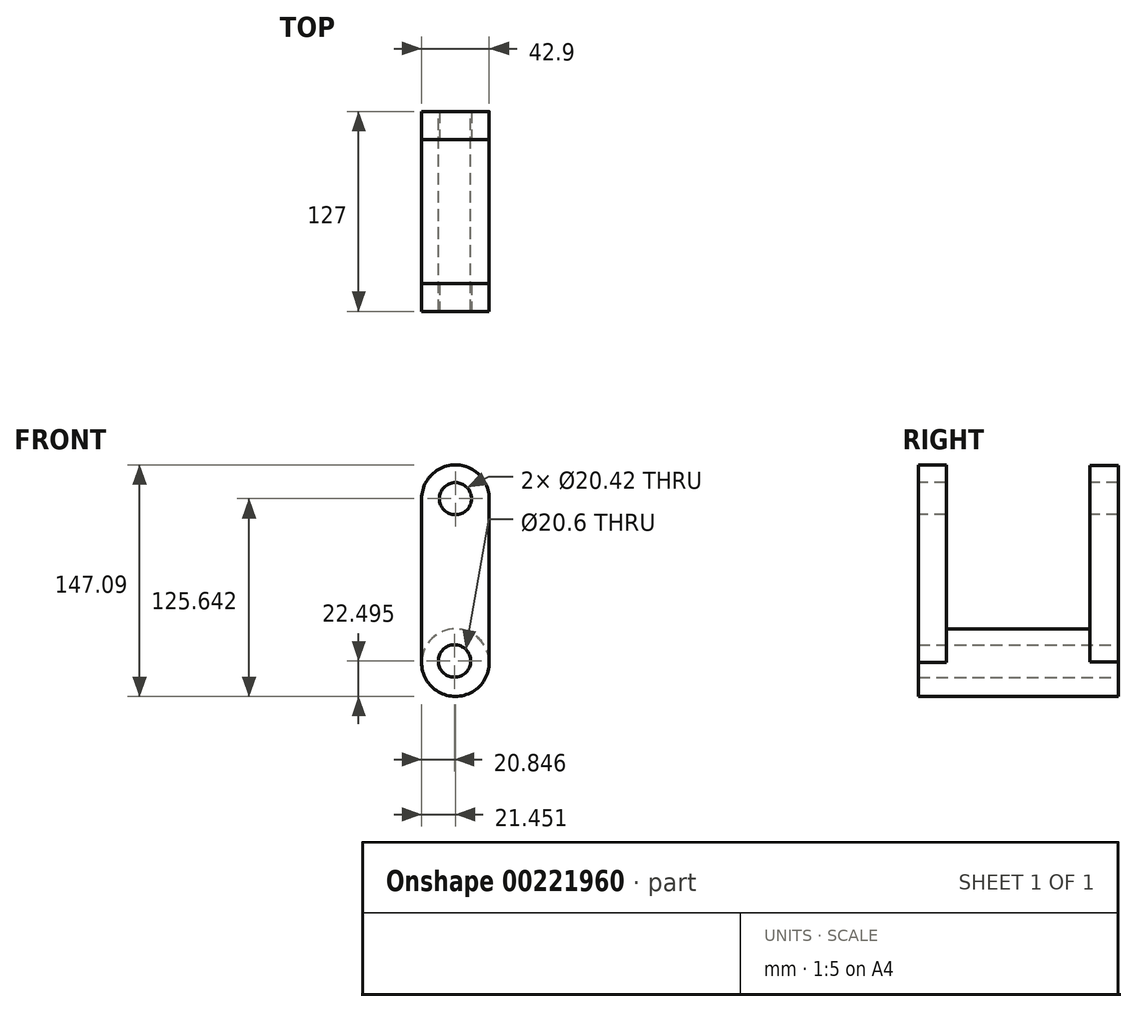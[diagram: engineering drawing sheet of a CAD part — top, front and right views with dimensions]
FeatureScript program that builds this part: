
annotation { "Feature Type Name" : "Feature", "Feature Type Description" : "" }
export const myFeature = defineFeature(function(context is Context, id is Id, definition is map)
    precondition{}
    {
        {
            var Q0;
            Q0=qCreatedBy(makeId("Front.planeOp"),FACE);
            var sketch = newSketch(context, id + "F0", { "sketchPlane" : qUnion([Q0])});
            skCircle(sketch, "E0", {"center": v(25.16, 31.72) * mm, "radius": 21.42 * mm});
            skSolve(sketch);
        }
        {
            var Q0;
            Q0 = qSketchRegion(id + "F0", true);
            extrude(context, id + "F1", {"entities" : qUnion([Q0]), "depth" : 127 * mm});
        }
        {
            var Q0;
            Q0=makeQuery(id+"F1.opExtrude","CAP_FACE",FACE,{"disambiguationData":[OSD([sQuery(id+"F0.wireOp",EDGE,"E0")])],"isStart":true});
            var sketch = newSketch(context, id + "F2", { "sketchPlane" : qUnion([Q0])});
            skLineSegment(sketch, "E1", {"start": v(-3.75, 32.24) * mm, "end": v(-46.57, 32.24) * mm});
            skLineSegment(sketch, "E2", {"start": v(-46.57, 32.24) * mm, "end": v(-46.57, 135.51) * mm});
            skLineSegment(sketch, "E3", {"start": v(-46.57, 135.51) * mm, "end": v(-3.75, 135.51) * mm});
            skLineSegment(sketch, "E4", {"start": v(-3.75, 135.51) * mm, "end": v(-3.75, 32.24) * mm});
            skSolve(sketch);
        }
        {
            var Q0;
            Q0 = qSketchRegion(id + "F2", true);
            extrude(context, id + "F3", {"entities" : qUnion([Q0]), "operationType" : NewBodyOperationType.ADD, "oppositeDirection" : true, "depth" : 17.78 * mm});
        }
        {
            var Q0;
            Q0=makeQuery(id+"F1.opExtrude","CAP_FACE",FACE,{"disambiguationData":[OSD([sQuery(id+"F0.wireOp",EDGE,"E0")])],"isStart":false});
            var sketch = newSketch(context, id + "F4", { "sketchPlane" : qUnion([Q0])});
            skLineSegment(sketch, "E5", {"start": v(46.58, 31.96) * mm, "end": v(3.75, 31.96) * mm});
            skLineSegment(sketch, "E6", {"start": v(3.75, 31.96) * mm, "end": v(3.75, 135.93) * mm});
            skLineSegment(sketch, "E7", {"start": v(3.75, 135.93) * mm, "end": v(46.64, 135.93) * mm});
            skLineSegment(sketch, "E8", {"start": v(46.64, 135.93) * mm, "end": v(46.58, 31.96) * mm});
            skSolve(sketch);
        }
        {
            var Q0;
            Q0 = qSketchRegion(id + "F4", true);
            extrude(context, id + "F5", {"entities" : qUnion([Q0]), "operationType" : NewBodyOperationType.ADD, "oppositeDirection" : true, "depth" : 17.78 * mm});
        }
        {
            var Q0;
            Q0=qCreatedBy(makeId("Front.planeOp"),FACE);
            var sketch = newSketch(context, id + "F6", { "sketchPlane" : qUnion([Q0])});
            skCircle(sketch, "E9", {"center": v(25.24, 31.5) * mm, "radius": 7.37 * mm});
            skSolve(sketch);
        }
        {
            var Q0;
            Q0 = qSketchRegion(id + "F6", true);
            extrude(context, id + "F7", {"entities" : qUnion([Q0]), "operationType" : NewBodyOperationType.REMOVE, "endBound" : BoundingType.THROUGH_ALL, "oppositeDirection" : true, "depth" : 25.4 * mm});
        }
        {
            var Q0;
            Q0=qCreatedBy(makeId("Front.planeOp"),FACE);
            var sketch = newSketch(context, id + "F8", { "sketchPlane" : qUnion([Q0])});
            skCircle(sketch, "E10", {"center": v(24.59, 32.8) * mm, "radius": 10.3 * mm});
            skSolve(sketch);
        }
        {
            var Q0;
            Q0 = qSketchRegion(id + "F8", true);
            extrude(context, id + "F9", {"entities" : qUnion([Q0]), "operationType" : NewBodyOperationType.REMOVE, "endBound" : BoundingType.THROUGH_ALL, "depth" : 25.4 * mm});
        }
        {
            var Q0;
            Q0=makeQuery(id+"F5.boolean.opBoolean","MERGE",FACE,{"derivedFrom":[makeQuery(id+"F1.opExtrude","CAP_FACE",FACE,{"disambiguationData":[OSD([sQuery(id+"F0.wireOp",EDGE,"E0")])],"isStart":false}),makeQuery(id+"F5.opExtrude","CAP_FACE",FACE,{"disambiguationData":[OSD([sQuery(id+"F4.wireOp",EDGE,"E5"),sQuery(id+"F4.wireOp",EDGE,"E6"),sQuery(id+"F4.wireOp",EDGE,"E7"),sQuery(id+"F4.wireOp",EDGE,"E8")])],"isStart":true})]});
            var sketch = newSketch(context, id + "F10", { "sketchPlane" : qUnion([Q0])});
            skArc(sketch, "E11", {"start": v(46.64, 135.93) * mm, "mid": v(25.2, 157.39) * mm, "end": v(3.75, 135.93) * mm});
            skLineSegment(sketch, "E12", {"start": v(3.75, 135.93) * mm, "end": v(46.64, 135.93) * mm});
            skSolve(sketch);
        }
        {
            var Q0;
            Q0 = qSketchRegion(id + "F10", true);
            extrude(context, id + "F11", {"entities" : qUnion([Q0]), "operationType" : NewBodyOperationType.ADD, "oppositeDirection" : true, "depth" : 17.78 * mm});
        }
        {
            var Q0;
            Q0=makeQuery(id+"F3.boolean.opBoolean","MERGE",FACE,{"derivedFrom":[makeQuery(id+"F1.opExtrude","CAP_FACE",FACE,{"disambiguationData":[OSD([sQuery(id+"F0.wireOp",EDGE,"E0")])],"isStart":true}),makeQuery(id+"F3.opExtrude","CAP_FACE",FACE,{"disambiguationData":[OSD([sQuery(id+"F2.wireOp",EDGE,"E1"),sQuery(id+"F2.wireOp",EDGE,"E2"),sQuery(id+"F2.wireOp",EDGE,"E3"),sQuery(id+"F2.wireOp",EDGE,"E4")])],"isStart":true})]});
            var sketch = newSketch(context, id + "F12", { "sketchPlane" : qUnion([Q0])});
            skArc(sketch, "E13", {"start": v(-3.75, 135.51) * mm, "mid": v(-25.16, 156.92) * mm, "end": v(-46.57, 135.51) * mm});
            skLineSegment(sketch, "E14", {"start": v(-46.57, 135.51) * mm, "end": v(-3.75, 135.51) * mm});
            skSolve(sketch);
        }
        {
            var Q0;
            Q0 = qSketchRegion(id + "F12", true);
            extrude(context, id + "F13", {"entities" : qUnion([Q0]), "operationType" : NewBodyOperationType.ADD, "oppositeDirection" : true, "depth" : 17.78 * mm});
        }
        {
            var Q0;
            Q0=makeQuery(id+"F11.boolean.opBoolean","MERGE",FACE,{"derivedFrom":[makeQuery(id+"F5.boolean.opBoolean","MERGE",FACE,{"derivedFrom":[makeQuery(id+"F1.opExtrude","CAP_FACE",FACE,{"disambiguationData":[OSD([sQuery(id+"F0.wireOp",EDGE,"E0")])],"isStart":false}),makeQuery(id+"F5.opExtrude","CAP_FACE",FACE,{"disambiguationData":[OSD([sQuery(id+"F4.wireOp",EDGE,"E5"),sQuery(id+"F4.wireOp",EDGE,"E6"),sQuery(id+"F4.wireOp",EDGE,"E7"),sQuery(id+"F4.wireOp",EDGE,"E8")])],"isStart":true})]}),makeQuery(id+"F11.opExtrude","CAP_FACE",FACE,{"disambiguationData":[OSD([sQuery(id+"F10.wireOp",EDGE,"E11"),sQuery(id+"F10.wireOp",EDGE,"E12")])],"isStart":true})]});
            var sketch = newSketch(context, id + "F14", { "sketchPlane" : qUnion([Q0])});
            skCircle(sketch, "E15", {"center": v(25.2, 135.94) * mm, "radius": 10.2 * mm});
            skSolve(sketch);
        }
        {
            var Q0;
            Q0 = qSketchRegion(id + "F14", true);
            extrude(context, id + "F15", {"entities" : qUnion([Q0]), "operationType" : NewBodyOperationType.REMOVE, "endBound" : BoundingType.THROUGH_ALL, "oppositeDirection" : true, "depth" : 25.4 * mm});
        }
    });
